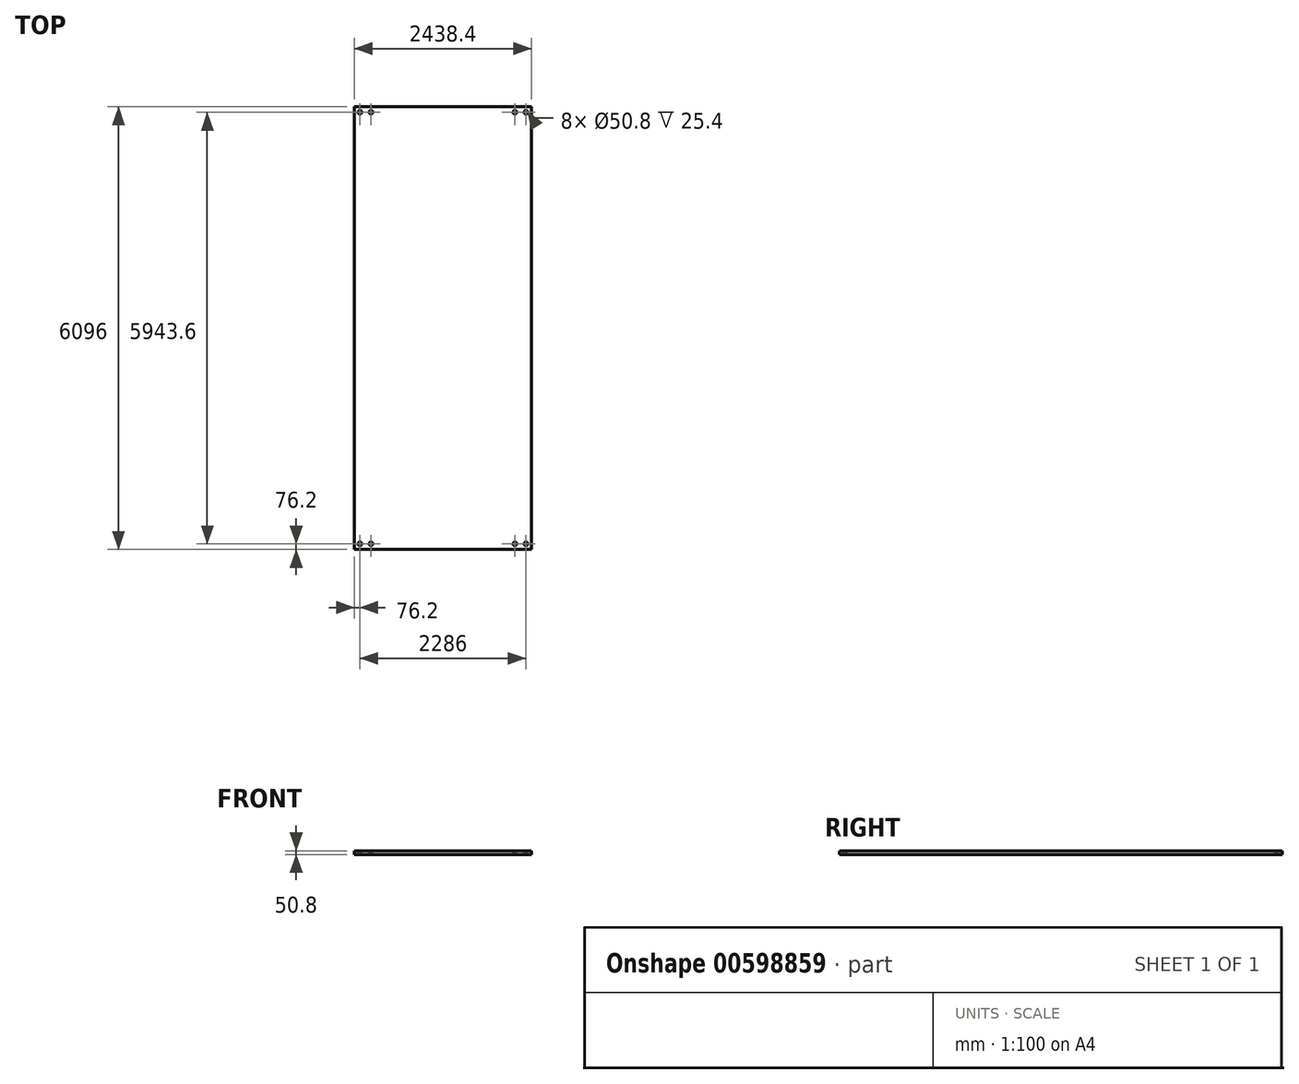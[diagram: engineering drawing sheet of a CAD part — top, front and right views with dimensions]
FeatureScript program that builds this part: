
annotation { "Feature Type Name" : "Feature", "Feature Type Description" : "" }
export const myFeature = defineFeature(function(context is Context, id is Id, definition is map)
    precondition{}
    {
        {
            var Q0;
            Q0=qCreatedBy(makeId("Top.planeOp"),FACE);
            var sketch = newSketch(context, id + "F0", { "sketchPlane" : qUnion([Q0])});
            skLineSegment(sketch, "E0.bottom", {"start": v(1219.2, 3048) * mm, "end": v(-1219.2, 3048) * mm});
            skLineSegment(sketch, "E0.top", {"start": v(1219.2, -3048) * mm, "end": v(-1219.2, -3048) * mm});
            skLineSegment(sketch, "E0.left", {"start": v(1219.2, 3048) * mm, "end": v(1219.2, -3048) * mm});
            skLineSegment(sketch, "E0.right", {"start": v(-1219.2, 3048) * mm, "end": v(-1219.2, -3048) * mm});
            skPoint(sketch, "E0.middle", {"position": v(0, 0) * mm});
            skSolve(sketch);
        }
        {
            var Q0;
            Q0=makeQuery(id+"F0.imprint","IMPRINT",FACE,{"disambiguationData":[TD([[makeQuery(id+"F0.imprint","IMPRINT",EDGE,{"derivedFrom":sQuery(id+"F0.wireOp",EDGE,"E0.bottom")}),1.0]])]});
            extrude(context, id + "F1", {"entities" : qUnion([Q0]), "depth" : 50.8 * mm, "offsetDistance" : 25.4 * mm});
        }
        {
            var Q0;
            Q0=makeQuery(id+"F1.opExtrude","CAP_FACE",FACE,{"disambiguationData":[OSD([sQuery(id+"F0.wireOp",EDGE,"E0.bottom"),sQuery(id+"F0.wireOp",EDGE,"E0.top"),sQuery(id+"F0.wireOp",EDGE,"E0.left"),sQuery(id+"F0.wireOp",EDGE,"E0.right")])],"isStart":false});
            var sketch = newSketch(context, id + "F2", { "sketchPlane" : qUnion([Q0])});
            skLineSegment(sketch, "E1.bottom", {"start": v(1219.2, -3048) * mm, "end": v(1143, -3048) * mm});
            skLineSegment(sketch, "E1.top", {"start": v(1219.2, -2971.8) * mm, "end": v(1143, -2971.8) * mm});
            skLineSegment(sketch, "E1.left", {"start": v(1219.2, -3048) * mm, "end": v(1219.2, -2971.8) * mm});
            skLineSegment(sketch, "E1.right", {"start": v(1143, -3048) * mm, "end": v(1143, -2971.8) * mm});
            skLineSegment(sketch, "E2.bottom", {"start": v(-1219.2, -3048) * mm, "end": v(-1143, -3048) * mm});
            skLineSegment(sketch, "E2.top", {"start": v(-1219.2, -2971.8) * mm, "end": v(-1143, -2971.8) * mm});
            skLineSegment(sketch, "E2.left", {"start": v(-1219.2, -3048) * mm, "end": v(-1219.2, -2971.8) * mm});
            skLineSegment(sketch, "E2.right", {"start": v(-1143, -3048) * mm, "end": v(-1143, -2971.8) * mm});
            skLineSegment(sketch, "E3.bottom", {"start": v(1219.2, 3048) * mm, "end": v(1143, 3048) * mm});
            skLineSegment(sketch, "E3.top", {"start": v(1219.2, 2971.8) * mm, "end": v(1143, 2971.8) * mm});
            skLineSegment(sketch, "E3.left", {"start": v(1219.2, 3048) * mm, "end": v(1219.2, 2971.8) * mm});
            skLineSegment(sketch, "E3.right", {"start": v(1143, 3048) * mm, "end": v(1143, 2971.8) * mm});
            skLineSegment(sketch, "E4.bottom", {"start": v(-1219.2, 3048) * mm, "end": v(-1143, 3048) * mm});
            skLineSegment(sketch, "E4.top", {"start": v(-1219.2, 2971.8) * mm, "end": v(-1143, 2971.8) * mm});
            skLineSegment(sketch, "E4.left", {"start": v(-1219.2, 3048) * mm, "end": v(-1219.2, 2971.8) * mm});
            skLineSegment(sketch, "E4.right", {"start": v(-1143, 3048) * mm, "end": v(-1143, 2971.8) * mm});
            skCircle(sketch, "E5", {"center": v(-1143, 2971.8) * mm, "radius": 25.4 * mm});
            skCircle(sketch, "E6", {"center": v(1143, 2971.8) * mm, "radius": 25.4 * mm});
            skCircle(sketch, "E7", {"center": v(1143, -2971.8) * mm, "radius": 25.4 * mm});
            skCircle(sketch, "E8", {"center": v(-1143, -2971.8) * mm, "radius": 25.4 * mm});
            skSolve(sketch);
        }
        {
            var Q0;
            {var subQ0=sQuery(id+"F2.wireOp",EDGE,"E3.right");var subQ1=sQuery(id+"F2.wireOp",EDGE,"E3.top");var subQ2=makeQuery(id+"F2.imprint","INTERSECT",VERTEX,{"derivedFrom":[subQ1,subQ0]});Q0=makeQuery(id+"F2.imprint","IMPRINT",FACE,{"disambiguationData":[TD([[makeQuery(id+"F2.imprint","IMPRINT",EDGE,{"disambiguationData":[TD([[subQ2,1.0]])],"derivedFrom":subQ1}),-1.0]])]});}
            var Q1;
            {var subQ0=sQuery(id+"F2.wireOp",EDGE,"E3.right");var subQ1=sQuery(id+"F2.wireOp",EDGE,"E3.top");var subQ2=makeQuery(id+"F2.imprint","INTERSECT",VERTEX,{"derivedFrom":[subQ1,subQ0]});Q1=makeQuery(id+"F2.imprint","IMPRINT",FACE,{"disambiguationData":[TD([[makeQuery(id+"F2.imprint","IMPRINT",EDGE,{"disambiguationData":[TD([[subQ2,1.0]])],"derivedFrom":subQ1}),1.0]])]});}
            var Q2;
            {var subQ0=sQuery(id+"F2.wireOp",EDGE,"E1.right");var subQ1=sQuery(id+"F2.wireOp",EDGE,"E1.top");var subQ2=makeQuery(id+"F2.imprint","INTERSECT",VERTEX,{"derivedFrom":[subQ1,subQ0]});Q2=makeQuery(id+"F2.imprint","IMPRINT",FACE,{"disambiguationData":[TD([[makeQuery(id+"F2.imprint","IMPRINT",EDGE,{"disambiguationData":[TD([[subQ2,1.0]])],"derivedFrom":subQ1}),1.0]])]});}
            var Q3;
            {var subQ0=sQuery(id+"F2.wireOp",EDGE,"E1.right");var subQ1=sQuery(id+"F2.wireOp",EDGE,"E1.top");var subQ2=makeQuery(id+"F2.imprint","INTERSECT",VERTEX,{"derivedFrom":[subQ1,subQ0]});Q3=makeQuery(id+"F2.imprint","IMPRINT",FACE,{"disambiguationData":[TD([[makeQuery(id+"F2.imprint","IMPRINT",EDGE,{"disambiguationData":[TD([[subQ2,1.0]])],"derivedFrom":subQ1}),-1.0]])]});}
            var Q4;
            {var subQ0=sQuery(id+"F2.wireOp",EDGE,"E2.right");var subQ1=sQuery(id+"F2.wireOp",EDGE,"E2.top");var subQ2=makeQuery(id+"F2.imprint","INTERSECT",VERTEX,{"derivedFrom":[subQ1,subQ0]});Q4=makeQuery(id+"F2.imprint","IMPRINT",FACE,{"disambiguationData":[TD([[makeQuery(id+"F2.imprint","IMPRINT",EDGE,{"disambiguationData":[TD([[subQ2,1.0]])],"derivedFrom":subQ1}),-1.0]])]});}
            var Q5;
            {var subQ0=sQuery(id+"F2.wireOp",EDGE,"E2.right");var subQ1=sQuery(id+"F2.wireOp",EDGE,"E2.top");var subQ2=makeQuery(id+"F2.imprint","INTERSECT",VERTEX,{"derivedFrom":[subQ1,subQ0]});Q5=makeQuery(id+"F2.imprint","IMPRINT",FACE,{"disambiguationData":[TD([[makeQuery(id+"F2.imprint","IMPRINT",EDGE,{"disambiguationData":[TD([[subQ2,1.0]])],"derivedFrom":subQ1}),1.0]])]});}
            var Q6;
            {var subQ0=sQuery(id+"F2.wireOp",EDGE,"E4.right");var subQ1=sQuery(id+"F2.wireOp",EDGE,"E4.top");var subQ2=makeQuery(id+"F2.imprint","INTERSECT",VERTEX,{"derivedFrom":[subQ1,subQ0]});Q6=makeQuery(id+"F2.imprint","IMPRINT",FACE,{"disambiguationData":[TD([[makeQuery(id+"F2.imprint","IMPRINT",EDGE,{"disambiguationData":[TD([[subQ2,1.0]])],"derivedFrom":subQ1}),1.0]])]});}
            var Q7;
            {var subQ0=sQuery(id+"F2.wireOp",EDGE,"E4.right");var subQ1=sQuery(id+"F2.wireOp",EDGE,"E4.top");var subQ2=makeQuery(id+"F2.imprint","INTERSECT",VERTEX,{"derivedFrom":[subQ1,subQ0]});Q7=makeQuery(id+"F2.imprint","IMPRINT",FACE,{"disambiguationData":[TD([[makeQuery(id+"F2.imprint","IMPRINT",EDGE,{"disambiguationData":[TD([[subQ2,1.0]])],"derivedFrom":subQ1}),-1.0]])]});}
            extrude(context, id + "F3", {"entities" : qUnion([Q0, Q1, Q2, Q3, Q4, Q5, Q6, Q7]), "operationType" : NewBodyOperationType.REMOVE, "oppositeDirection" : true, "depth" : 25.4 * mm, "offsetDistance" : 25.4 * mm});
        }
        {
            var Q0;
            Q0=makeQuery(id+"F1.opExtrude","CAP_FACE",FACE,{"disambiguationData":[OSD([sQuery(id+"F0.wireOp",EDGE,"E0.bottom"),sQuery(id+"F0.wireOp",EDGE,"E0.top"),sQuery(id+"F0.wireOp",EDGE,"E0.left"),sQuery(id+"F0.wireOp",EDGE,"E0.right")])],"isStart":false});
            var sketch = newSketch(context, id + "F4", { "sketchPlane" : qUnion([Q0])});
            skLineSegment(sketch, "E9.bottom", {"start": v(-1219.2, 3048) * mm, "end": v(-990.6, 3048) * mm});
            skLineSegment(sketch, "E9.top", {"start": v(-1219.2, 2971.8) * mm, "end": v(-990.6, 2971.8) * mm});
            skLineSegment(sketch, "E9.left", {"start": v(-1219.2, 3048) * mm, "end": v(-1219.2, 2971.8) * mm});
            skLineSegment(sketch, "E9.right", {"start": v(-990.6, 3048) * mm, "end": v(-990.6, 2971.8) * mm});
            skCircle(sketch, "E10", {"center": v(-990.6, 2971.8) * mm, "radius": 25.4 * mm});
            skLineSegment(sketch, "E11.bottom", {"start": v(1219.2, 3048) * mm, "end": v(990.6, 3048) * mm});
            skLineSegment(sketch, "E11.top", {"start": v(1219.2, 2971.8) * mm, "end": v(990.6, 2971.8) * mm});
            skLineSegment(sketch, "E11.left", {"start": v(1219.2, 3048) * mm, "end": v(1219.2, 2971.8) * mm});
            skLineSegment(sketch, "E11.right", {"start": v(990.6, 3048) * mm, "end": v(990.6, 2971.8) * mm});
            skCircle(sketch, "E12", {"center": v(990.6, 2971.8) * mm, "radius": 25.4 * mm});
            skLineSegment(sketch, "E13.bottom", {"start": v(-1219.2, -3048) * mm, "end": v(-990.6, -3048) * mm});
            skLineSegment(sketch, "E13.top", {"start": v(-1219.2, -2971.8) * mm, "end": v(-990.6, -2971.8) * mm});
            skLineSegment(sketch, "E13.left", {"start": v(-1219.2, -3048) * mm, "end": v(-1219.2, -2971.8) * mm});
            skLineSegment(sketch, "E13.right", {"start": v(-990.6, -3048) * mm, "end": v(-990.6, -2971.8) * mm});
            skLineSegment(sketch, "E14.bottom", {"start": v(1219.2, -3048) * mm, "end": v(990.6, -3048) * mm});
            skLineSegment(sketch, "E14.top", {"start": v(1219.2, -2971.8) * mm, "end": v(990.6, -2971.8) * mm});
            skLineSegment(sketch, "E14.left", {"start": v(1219.2, -3048) * mm, "end": v(1219.2, -2971.8) * mm});
            skLineSegment(sketch, "E14.right", {"start": v(990.6, -3048) * mm, "end": v(990.6, -2971.8) * mm});
            skCircle(sketch, "E15", {"center": v(-990.6, -2971.8) * mm, "radius": 25.4 * mm});
            skCircle(sketch, "E16", {"center": v(990.6, -2971.8) * mm, "radius": 25.4 * mm});
            skSolve(sketch);
        }
        {
            var Q0;
            {var subQ0=sQuery(id+"F4.wireOp",EDGE,"E14.right");var subQ1=sQuery(id+"F4.wireOp",EDGE,"E14.top");var subQ2=makeQuery(id+"F4.imprint","INTERSECT",VERTEX,{"derivedFrom":[subQ1,subQ0]});Q0=makeQuery(id+"F4.imprint","IMPRINT",FACE,{"disambiguationData":[TD([[makeQuery(id+"F4.imprint","IMPRINT",EDGE,{"disambiguationData":[TD([[subQ2,1.0]])],"derivedFrom":subQ1}),-1.0]])]});}
            var Q1;
            {var subQ0=sQuery(id+"F4.wireOp",EDGE,"E14.right");var subQ1=sQuery(id+"F4.wireOp",EDGE,"E14.top");var subQ2=makeQuery(id+"F4.imprint","INTERSECT",VERTEX,{"derivedFrom":[subQ1,subQ0]});Q1=makeQuery(id+"F4.imprint","IMPRINT",FACE,{"disambiguationData":[TD([[makeQuery(id+"F4.imprint","IMPRINT",EDGE,{"disambiguationData":[TD([[subQ2,1.0]])],"derivedFrom":subQ1}),1.0]])]});}
            var Q2;
            {var subQ0=sQuery(id+"F4.wireOp",EDGE,"E13.right");var subQ1=sQuery(id+"F4.wireOp",EDGE,"E13.top");var subQ2=makeQuery(id+"F4.imprint","INTERSECT",VERTEX,{"derivedFrom":[subQ1,subQ0]});Q2=makeQuery(id+"F4.imprint","IMPRINT",FACE,{"disambiguationData":[TD([[makeQuery(id+"F4.imprint","IMPRINT",EDGE,{"disambiguationData":[TD([[subQ2,1.0]])],"derivedFrom":subQ1}),-1.0]])]});}
            var Q3;
            {var subQ0=sQuery(id+"F4.wireOp",EDGE,"E13.right");var subQ1=sQuery(id+"F4.wireOp",EDGE,"E13.top");var subQ2=makeQuery(id+"F4.imprint","INTERSECT",VERTEX,{"derivedFrom":[subQ1,subQ0]});Q3=makeQuery(id+"F4.imprint","IMPRINT",FACE,{"disambiguationData":[TD([[makeQuery(id+"F4.imprint","IMPRINT",EDGE,{"disambiguationData":[TD([[subQ2,1.0]])],"derivedFrom":subQ1}),1.0]])]});}
            var Q4;
            {var subQ0=sQuery(id+"F4.wireOp",EDGE,"E11.right");var subQ1=sQuery(id+"F4.wireOp",EDGE,"E11.top");var subQ2=makeQuery(id+"F4.imprint","INTERSECT",VERTEX,{"derivedFrom":[subQ1,subQ0]});Q4=makeQuery(id+"F4.imprint","IMPRINT",FACE,{"disambiguationData":[TD([[makeQuery(id+"F4.imprint","IMPRINT",EDGE,{"disambiguationData":[TD([[subQ2,1.0]])],"derivedFrom":subQ1}),-1.0]])]});}
            var Q5;
            {var subQ0=sQuery(id+"F4.wireOp",EDGE,"E11.right");var subQ1=sQuery(id+"F4.wireOp",EDGE,"E11.top");var subQ2=makeQuery(id+"F4.imprint","INTERSECT",VERTEX,{"derivedFrom":[subQ1,subQ0]});Q5=makeQuery(id+"F4.imprint","IMPRINT",FACE,{"disambiguationData":[TD([[makeQuery(id+"F4.imprint","IMPRINT",EDGE,{"disambiguationData":[TD([[subQ2,1.0]])],"derivedFrom":subQ1}),1.0]])]});}
            var Q6;
            {var subQ0=sQuery(id+"F4.wireOp",EDGE,"E9.right");var subQ1=sQuery(id+"F4.wireOp",EDGE,"E9.top");var subQ2=makeQuery(id+"F4.imprint","INTERSECT",VERTEX,{"derivedFrom":[subQ1,subQ0]});Q6=makeQuery(id+"F4.imprint","IMPRINT",FACE,{"disambiguationData":[TD([[makeQuery(id+"F4.imprint","IMPRINT",EDGE,{"disambiguationData":[TD([[subQ2,1.0]])],"derivedFrom":subQ1}),1.0]])]});}
            var Q7;
            {var subQ0=sQuery(id+"F4.wireOp",EDGE,"E9.right");var subQ1=sQuery(id+"F4.wireOp",EDGE,"E9.top");var subQ2=makeQuery(id+"F4.imprint","INTERSECT",VERTEX,{"derivedFrom":[subQ1,subQ0]});Q7=makeQuery(id+"F4.imprint","IMPRINT",FACE,{"disambiguationData":[TD([[makeQuery(id+"F4.imprint","IMPRINT",EDGE,{"disambiguationData":[TD([[subQ2,1.0]])],"derivedFrom":subQ1}),-1.0]])]});}
            extrude(context, id + "F5", {"entities" : qUnion([Q0, Q1, Q2, Q3, Q4, Q5, Q6, Q7]), "operationType" : NewBodyOperationType.REMOVE, "oppositeDirection" : true, "depth" : 25.4 * mm, "offsetDistance" : 25.4 * mm});
        }
    });
